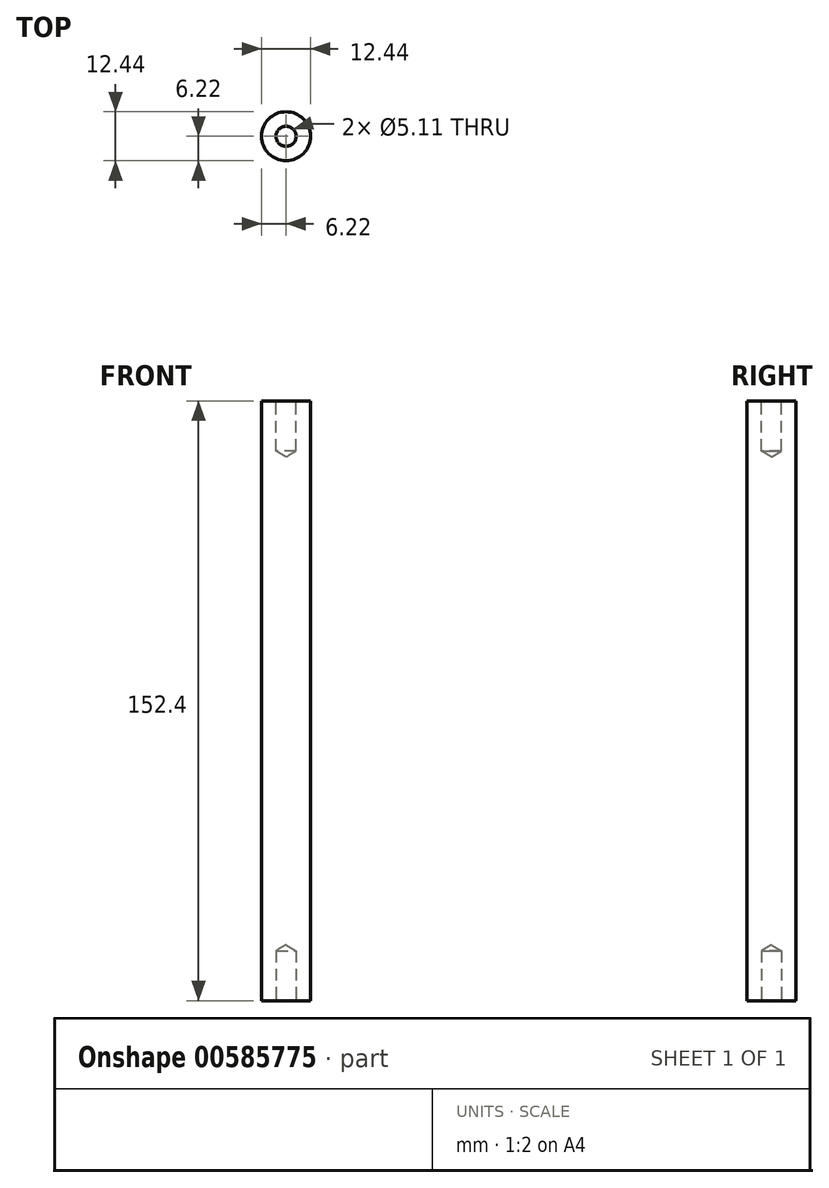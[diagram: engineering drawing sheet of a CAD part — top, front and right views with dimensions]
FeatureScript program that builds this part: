
annotation { "Feature Type Name" : "Feature", "Feature Type Description" : "" }
export const myFeature = defineFeature(function(context is Context, id is Id, definition is map)
    precondition{}
    {
        {
            var Q0;
            Q0=qCreatedBy(makeId("Top.planeOp"),FACE);
            var sketch = newSketch(context, id + "F0", { "sketchPlane" : qUnion([Q0])});
            skCircle(sketch, "E0", {"center": v(0, 0) * mm, "radius": 6.22 * mm});
            skSolve(sketch);
        }
        {
            var Q0;
            Q0=makeQuery(id+"F0.imprint","IMPRINT",FACE,{"disambiguationData":[TD([[makeQuery(id+"F0.imprint","IMPRINT",EDGE,{"derivedFrom":sQuery(id+"F0.wireOp",EDGE,"E0")}),1.0]])]});
            extrude(context, id + "F1", {"entities" : qUnion([Q0]), "oppositeDirection" : true, "depth" : 152.4 * mm});
        }
        {
            var Q0;
            Q0=makeQuery(id+"F1.opExtrude","CAP_FACE",FACE,{"disambiguationData":[OSD([sQuery(id+"F0.wireOp",EDGE,"E0")])],"isStart":false});
            var sketch = newSketch(context, id + "F2", { "sketchPlane" : qUnion([Q0])});
            skPoint(sketch, "E1", {"position": v(0, 0) * mm});
            skSolve(sketch);
        }
        {
            var Q0;
            Q0=sQuery(id+"F2.wireOp",VERTEX,"E1");
            var Q1;
            Q1=makeQuery(id+"F1.opExtrude","SWEPT_BODY",BODY,{"disambiguationData":[OSD([sQuery(id+"F0.wireOp",EDGE,"E0")])]});
            hole(context, id + "F3", {"style" : HoleStyle.SIMPLE, "endStyle" : HoleEndStyle.BLIND, "standardTappedOrClearance" : lookupTablePath({ "standard" : "ANSI", "engagement" : "75%", "pitch" : "20 tpi", "size" : "1/4", "type" : "Tapped" }), "standardBlindInLast" : lookupTablePath({ "standard" : "ANSI", "engagement" : "75%", "pitch" : "20 tpi", "size" : "1/4", "type" : "Tapped" }), "holeDiameter" : 5.1 * mm, "showTappedDepth" : true, "holeDepth" : 12.7 * mm, "isTappedThrough" : true, "tappedDepth" : 8.9 * mm, "tapClearance" : 3, "startFromSketch" : true, "locations" : qUnion([Q0]), "scope" : qUnion([Q1]), "majorDiameter" : 6.35 * mm});
        }
        {
            var Q0;
            Q0=makeQuery(id+"F1.opExtrude","CAP_FACE",FACE,{"disambiguationData":[OSD([sQuery(id+"F0.wireOp",EDGE,"E0")])],"isStart":true});
            var sketch = newSketch(context, id + "F4", { "sketchPlane" : qUnion([Q0])});
            skPoint(sketch, "E2", {"position": v(0, 0) * mm});
            skSolve(sketch);
        }
        {
            var Q0;
            Q0=sQuery(id+"F4.wireOp",VERTEX,"E2");
            var Q1;
            Q1=makeQuery(id+"F1.opExtrude","SWEPT_BODY",BODY,{"disambiguationData":[OSD([sQuery(id+"F0.wireOp",EDGE,"E0")])]});
            hole(context, id + "F5", {"style" : HoleStyle.SIMPLE, "endStyle" : HoleEndStyle.BLIND, "standardTappedOrClearance" : lookupTablePath({ "standard" : "ANSI", "engagement" : "75%", "pitch" : "20 tpi", "size" : "1/4", "type" : "Tapped" }), "standardBlindInLast" : lookupTablePath({ "standard" : "ANSI", "engagement" : "75%", "pitch" : "20 tpi", "size" : "1/4", "type" : "Tapped" }), "holeDiameter" : 5.1 * mm, "showTappedDepth" : true, "holeDepth" : 12.7 * mm, "isTappedThrough" : true, "tappedDepth" : 8.9 * mm, "tapClearance" : 3, "startFromSketch" : true, "locations" : qUnion([Q0]), "scope" : qUnion([Q1]), "majorDiameter" : 6.35 * mm});
        }
    });
